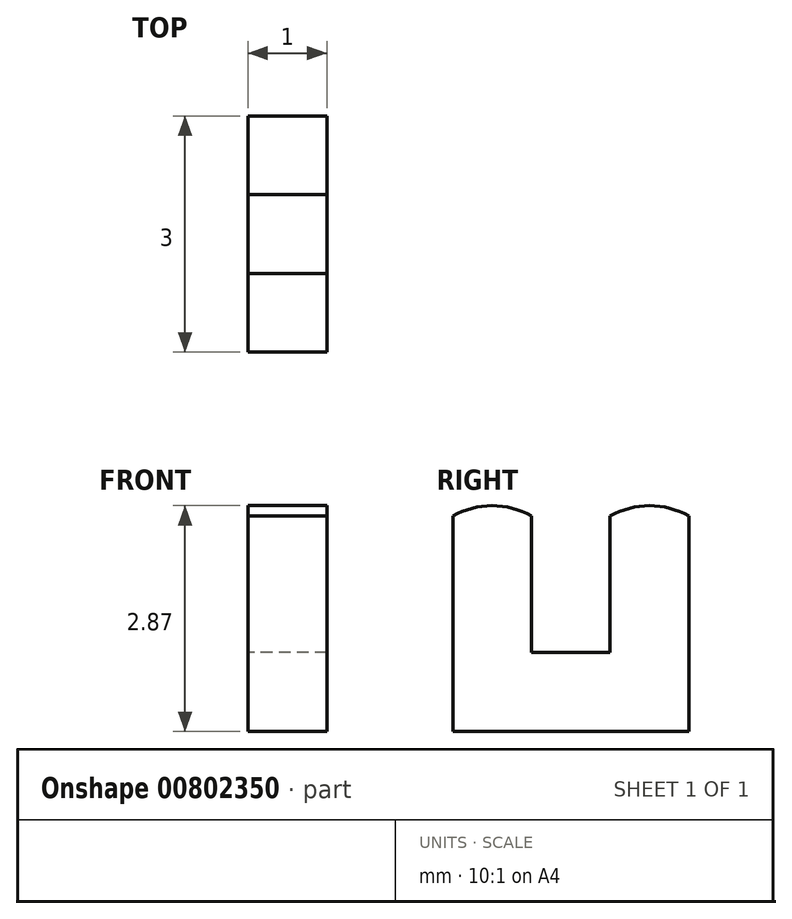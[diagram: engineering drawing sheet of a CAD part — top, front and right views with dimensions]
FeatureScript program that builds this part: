
annotation { "Feature Type Name" : "Feature", "Feature Type Description" : "" }
export const myFeature = defineFeature(function(context is Context, id is Id, definition is map)
    precondition{}
    {
        {
            var Q0;
            Q0=qCreatedBy(makeId("Right.planeOp"),FACE);
            var sketch = newSketch(context, id + "F0", { "sketchPlane" : qUnion([Q0])});
            skCircle(sketch, "E0", {"center": v(1, 0) * mm, "radius": 1 * mm, "construction": true});
            skArc(sketch, "E1", {"start": v(0.5, 0.87) * mm, "mid": v(0, 1) * mm, "end": v(-0.5, 0.87) * mm});
            skArc(sketch, "E2", {"start": v(0.5, -0.87) * mm, "mid": v(1, 0) * mm, "end": v(0.5, 0.87) * mm, "construction": true});
            skArc(sketch, "E3", {"start": v(1.5, 0.87) * mm, "mid": v(1, 0) * mm, "end": v(1.5, -0.87) * mm, "construction": true});
            skArc(sketch, "E4", {"start": v(1.5, -0.87) * mm, "mid": v(2, -1) * mm, "end": v(2.5, -0.87) * mm, "construction": true});
            skLineSegment(sketch, "E5", {"start": v(0.5, 0.87) * mm, "end": v(0.5, -0.87) * mm});
            skLineSegment(sketch, "E6", {"start": v(0.5, -0.87) * mm, "end": v(1.5, -0.87) * mm});
            skLineSegment(sketch, "E7", {"start": v(1.5, 0.87) * mm, "end": v(1.5, -0.87) * mm});
            skCircle(sketch, "E8", {"center": v(-1, 0) * mm, "radius": 1 * mm, "construction": true});
            skCircle(sketch, "E9", {"center": v(3, 0) * mm, "radius": 1 * mm, "construction": true});
            skArc(sketch, "E10", {"start": v(2.5, 0.87) * mm, "mid": v(2, 1) * mm, "end": v(1.5, 0.87) * mm});
            skArc(sketch, "E11", {"start": v(2.5, -0.87) * mm, "mid": v(3, 0) * mm, "end": v(2.5, 0.87) * mm, "construction": true});
            skArc(sketch, "E12", {"start": v(-0.5, 0.87) * mm, "mid": v(-1, 0) * mm, "end": v(-0.5, -0.87) * mm, "construction": true});
            skArc(sketch, "E13", {"start": v(-0.5, -0.87) * mm, "mid": v(0, -1) * mm, "end": v(0.5, -0.87) * mm, "construction": true});
            skLineSegment(sketch, "E14", {"start": v(-0.5, 0.87) * mm, "end": v(-0.5, -0.87) * mm});
            skLineSegment(sketch, "E15", {"start": v(2.5, 0.87) * mm, "end": v(2.5, -0.87) * mm});
            skLineSegment(sketch, "E16", {"start": v(-0.5, -0.87) * mm, "end": v(-0.5, -1.87) * mm});
            skLineSegment(sketch, "E17", {"start": v(-0.5, -1.87) * mm, "end": v(2.5, -1.87) * mm});
            skLineSegment(sketch, "E18", {"start": v(2.5, -1.87) * mm, "end": v(2.5, -0.87) * mm});
            skSolve(sketch);
        }
        {
            var Q0;
            Q0=makeQuery(id+"F0.imprint","IMPRINT",FACE,{"disambiguationData":[TD([[makeQuery(id+"F0.imprint","IMPRINT",EDGE,{"derivedFrom":sQuery(id+"F0.wireOp",EDGE,"E1")}),1.0]])]});
            extrude(context, id + "F1", {"entities" : qUnion([Q0]), "depth" : 1 * mm, "offsetDistance" : 25 * mm});
        }
    });
